FCSTD DOCUMENT  (FreeCAD 0.21R33668 +7 (Git))
Label: robot-main
License: All rights reserved
LicenseURL: https://en.wikipedia.org/wiki/All_rights_reserved
objects: App::Link×11
EXTERNAL_REF file=Off-the-shelf/BL-5C.FCStd obj=Body
EXTERNAL_REF file=robot-pcb.FCStd obj=LinkGroup
EXTERNAL_REF file=Off-the-shelf/GT2-220.FCStd obj=Body
EXTERNAL_REF file=Off-the-shelf/ball.FCStd obj=Body
EXTERNAL_REF file=robot-body.FCStd obj=Body
EXTERNAL_REF file=robot-idler.FCStd obj=LinkGroup
EXTERNAL_REF file=robot-motor-holder.FCStd obj=LinkGroup

FEATURE [App::Link] Link002  label="battery-t"
  LinkPlacement = pos=(-1.5,0,11.5) rot=(1,0,0;3.14159rad)
  LinkedObject = -> <external Off-the-shelf/BL-5C.FCStd>#Body
  Placement = pos=(-1.5,0,11.5) rot=(1,0,0;3.14159rad)
FEATURE [App::Link] Link003  label="battery-b"
  LinkPlacement = pos=(-1.5,0,-11.5) rot=(0,0,1;0rad)
  LinkedObject = -> <external Off-the-shelf/BL-5C.FCStd>#Body
  Placement = pos=(-1.5,0,-11.5) rot=(0,0,1;0rad)
FEATURE [App::Link] Link010  label="pcb"
  LinkPlacement = pos=(25,0,0) rot=(1,0,0;0rad)
  LinkedObject = -> <external robot-pcb.FCStd>#LinkGroup
  Placement = pos=(25,0,0) rot=(1,0,0;0rad)
FEATURE [App::Link] Link013  label="track-l"
  LinkPlacement = pos=(0,-30,0) rot=(0,0,1;0rad)
  LinkedObject = -> <external Off-the-shelf/GT2-220.FCStd>#Body
  Placement = pos=(0,-30,0) rot=(0,0,1;0rad)
FEATURE [App::Link] Link014  label="track-r"
  LinkPlacement = pos=(0,30,0) rot=(0,0,1;0rad)
  LinkedObject = -> <external Off-the-shelf/GT2-220.FCStd>#Body
  Placement = pos=(0,30,0) rot=(0,0,1;0rad)
FEATURE [App::Link] Link015  label="tt-ball"
  LinkPlacement = pos=(-40,0,0) rot=(0,0,1;0rad)
  LinkedObject = -> <external Off-the-shelf/ball.FCStd>#Body
  Placement = pos=(-40,0,0) rot=(0,0,1;0rad)
FEATURE [App::Link] Link016  label="body-main"
  LinkedObject = -> <external robot-body.FCStd>#Body
FEATURE [App::Link] Link019  label="idler-assy-l"
  LinkPlacement = pos=(50,-34,0) rot=(1,0,0;-1.5708rad)
  LinkedObject = -> <external robot-idler.FCStd>#LinkGroup
  Placement = pos=(50,-34,0) rot=(1,0,0;-1.5708rad)
FEATURE [App::Link] Link020  label="idler-assy-r"
  LinkPlacement = pos=(0,34,0) rot=(1,0,0;1.5708rad)
  LinkedObject = -> <external robot-idler.FCStd>#LinkGroup
  Placement = pos=(0,34,0) rot=(1,0,0;1.5708rad)
FEATURE [App::Link] Link  label="traction-assy-l"
  LinkPlacement = pos=(0,-14.9,0) rot=(0,0,1;0rad)
  LinkedObject = -> <external robot-motor-holder.FCStd>#LinkGroup
  Placement = pos=(0,-14.9,0) rot=(0,0,1;0rad)
FEATURE [App::Link] Link021  label="traction-assy-r"
  LinkPlacement = pos=(50,14.9,0) rot=(0,0,1;3.14159rad)
  LinkedObject = -> <external robot-motor-holder.FCStd>#LinkGroup
  Placement = pos=(50,14.9,0) rot=(0,0,1;3.14159rad)

RESOLVED EXTERNAL PARTS (link-assembly join: the EXTERNAL_REF files above that resolve inside this repo's crawl, each included once):
---- part Off-the-shelf/BL-5C.FCStd = doc fcstd_d717545ff7e7 ----
FCSTD DOCUMENT  (FreeCAD 0.21R33668 +7 (Git))
Label: BL-5C
License: All rights reserved
LicenseURL: https://en.wikipedia.org/wiki/All_rights_reserved
objects: Sketcher::SketchObject×2, PartDesign::Pad×1, PartDesign::Plane×1, PartDesign::Pocket×1, PartDesign::Body×1
note: 8 computed .brp shape members not serialized (recipe doc carries the construction recipe); baked Part::Feature solids carry a one-line shape summary decoded from their .brp

FEATURE [Sketcher::SketchObject] Sketch
  FullyConstrained = true
  MapMode = 5
  Placement = pos=(0,0,0) rot=(0.57735,0.57735,0.57735;2.0944rad)
  Support = -> [YZ_Plane]
  sketch-geometry (6):
    g0: ArcOfCircle CenterX=-14.15 CenterY=0 CenterZ=0 NormalX=0 NormalY=0 NormalZ=1 AngleXU=0 Radius=2.8 StartAngle=1.5708 EndAngle=4.71239
    g1: ArcOfCircle CenterX=14.15 CenterY=0 CenterZ=0 NormalX=0 NormalY=0 NormalZ=1 AngleXU=0 Radius=2.8 StartAngle=4.71239 EndAngle=7.85398
    g2: LineSegment StartX=-14.15 StartY=2.8 StartZ=0 EndX=14.15 EndY=2.8 EndZ=0
    g3: LineSegment StartX=-14.15 StartY=-2.8 StartZ=0 EndX=14.15 EndY=-2.8 EndZ=0
    g4: GeomPoint X=16.95 Y=0 Z=0
    g5: GeomPoint X=-16.95 Y=0 Z=0
  constraints (13):
    c: PointOnObject(g0,g-1)
    c: Horizontal(g2)
    c: Tangent(g2,g0) = 1.5708
    c: Tangent(g3,g0) = -1.5708
    c: Tangent(g3,g1) = -1.5708
    c: Tangent(g2,g1) = 1.5708
    c: PointOnObject(g4,g1)
    c: PointOnObject(g4,g-1)
    c: DistanceY(g1,g1) = 5.6
    c: Symmetric(g0,g1,g-1)
    c: PointOnObject(g5,g0)
    c: PointOnObject(g5,g-1)
    c: DistanceX(g5,g4) = 33.9
FEATURE [PartDesign::Pad] Pad
  Direction = (1,-2e-16,3e-16)
  Length = 53
  Length2 = 10
  Placement = pos=(0,0,0) rot=(0.57735,0.57735,0.57735;2.0944rad)
  Profile = -> Sketch
  ReferenceAxis = -> Sketch [N_Axis]
  Type = 0
FEATURE [PartDesign::Plane] DatumPlane
  Length = 60
  MapMode = 5
  Placement = pos=(0,0,0) rot=(0.57735,0.57735,-0.57735;4.18879rad)
  ResizeMode = 0
  Support = -> [Pad]
  Width = 60
FEATURE [Sketcher::SketchObject] Sketch001
  ExternalGeometry = -> [Pad]
  FullyConstrained = true
  MapMode = 5
  Placement = pos=(0,0,0) rot=(0.57735,0.57735,-0.57735;4.18879rad)
  Support = -> [DatumPlane]
  sketch-geometry (16):
    g0: LineSegment StartX=11.95 StartY=2.3 StartZ=0 EndX=13.95 EndY=2.3 EndZ=0
    g1: LineSegment StartX=13.95 StartY=2.3 StartZ=0 EndX=13.95 EndY=-2.3 EndZ=0
    g2: LineSegment StartX=13.95 StartY=-2.3 StartZ=0 EndX=11.95 EndY=-2.3 EndZ=0
    g3: LineSegment StartX=11.95 StartY=-2.3 StartZ=0 EndX=11.95 EndY=2.3 EndZ=0
    g4: LineSegment StartX=8.75 StartY=2.3 StartZ=0 EndX=10.75 EndY=2.3 EndZ=0
    g5: LineSegment StartX=10.75 StartY=2.3 StartZ=0 EndX=10.75 EndY=-2.3 EndZ=0
    g6: LineSegment StartX=10.75 StartY=-2.3 StartZ=0 EndX=8.75 EndY=-2.3 EndZ=0
    g7: LineSegment StartX=8.75 StartY=-2.3 StartZ=0 EndX=8.75 EndY=2.3 EndZ=0
    g8: LineSegment StartX=5.55 StartY=2.3 StartZ=0 EndX=7.55 EndY=2.3 EndZ=0
    g9: LineSegment StartX=7.55 StartY=2.3 StartZ=0 EndX=7.55 EndY=-2.3 EndZ=0
    g10: LineSegment StartX=7.55 StartY=-2.3 StartZ=0 EndX=5.55 EndY=-2.3 EndZ=0
    g11: LineSegment StartX=5.55 StartY=-2.3 StartZ=0 EndX=5.55 EndY=2.3 EndZ=0
    g12: LineSegment StartX=7.55 StartY=2.3 StartZ=0 EndX=8.75 EndY=2.3 EndZ=0
    g13: LineSegment StartX=10.75 StartY=2.3 StartZ=0 EndX=11.95 EndY=2.3 EndZ=0
    g14: GeomPoint X=-16.95 Y=0 Z=0
    g15: GeomPoint X=16.95 Y=0 Z=0
  constraints (43):
    c: Coincident(g0,g1)
    c: Coincident(g1,g2)
    c: Coincident(g2,g3)
    c: Coincident(g3,g0)
    c: Horizontal(g0)
    c: Horizontal(g2)
    c: Vertical(g3)
    c: Coincident(g4,g5)
    c: Coincident(g5,g6)
    c: Coincident(g6,g7)
    c: Coincident(g7,g4)
    c: Horizontal(g4)
    c: Horizontal(g6)
    c: Vertical(g5)
    c: Vertical(g7)
    c: Coincident(g8,g9)
    c: Coincident(g9,g10)
    c: Coincident(g10,g11)
    c: Coincident(g11,g8)
    c: Horizontal(g8)
    c: Horizontal(g10)
    c: Vertical(g9)
    c: Vertical(g11)
    c: PointOnObject(g4,g8)
    c: PointOnObject(g0,g8)
    c: PointOnObject(g6,g10)
    c: PointOnObject(g2,g10)
    c: Equal(g8,g4)
    c: Coincident(g12,g8)
    c: Coincident(g12,g4)
    c: Coincident(g13,g4)
    c: Coincident(g13,g0)
    c: Equal(g13,g12)
    c: PointOnObject(g14,g-3)
    c: PointOnObject(g14,g-1)
    c: DistanceX(g14,g10) = 22.5
    c: PointOnObject(g15,g-1)
    c: PointOnObject(g15,g-4)
    c: DistanceX(g1,g15) = 3
    c: DistanceX(g6,g6) = 2
    c: Equal(g2,g6)
    c: Symmetric(g0,g1,g-1)
    c: DistanceY(g1,g1) = 4.6
FEATURE [PartDesign::Pocket] Pocket
  BaseFeature = -> Pad
  Direction = (1,-4e-16,4e-16)
  Length = 0.6
  Length2 = 5
  Placement = pos=(0,0,0) rot=(0.57735,0.57735,0.57735;2.0944rad)
  Profile = -> Sketch001
  ReferenceAxis = -> Sketch001 [N_Axis]
  Type = 0
FEATURE [PartDesign::Body] Body  label="BL-5C"
  Group = -> [Sketch,Pad,DatumPlane,Sketch001,Pocket]
  Origin = -> Origin
  Tip = -> Pocket
---- part Off-the-shelf/GT2-220.FCStd = doc fcstd_4230f36f5c53 ----
FCSTD DOCUMENT  (FreeCAD 0.21R33668 +7 (Git))
Label: GT2-220
License: All rights reserved
LicenseURL: https://en.wikipedia.org/wiki/All_rights_reserved
objects: Sketcher::SketchObject×1, PartDesign::Pad×1, PartDesign::Body×1
note: 4 computed .brp shape members not serialized (recipe doc carries the construction recipe); baked Part::Feature solids carry a one-line shape summary decoded from their .brp

FEATURE [Sketcher::SketchObject] Sketch
  FullyConstrained = true
  MapMode = 5
  Placement = pos=(0,0,0) rot=(1,0,0;1.5708rad)
  Support = -> [XZ_Plane]
  sketch-geometry (10):
    g0: ArcOfCircle CenterX=0 CenterY=0 CenterZ=0 NormalX=0 NormalY=0 NormalZ=1 AngleXU=0 Radius=18 StartAngle=1.5708 EndAngle=4.71239
    g1: ArcOfCircle CenterX=47.6 CenterY=0 CenterZ=0 NormalX=0 NormalY=0 NormalZ=1 AngleXU=0 Radius=18 StartAngle=4.71239 EndAngle=7.85398
    g2: LineSegment StartX=1.1e-15 StartY=18 StartZ=0 EndX=47.6 EndY=18 EndZ=0
    g3: LineSegment StartX=-3.3e-15 StartY=-18 StartZ=0 EndX=47.6 EndY=-18 EndZ=0
    g4: Circle CenterX=0 CenterY=0 CenterZ=0 NormalX=0 NormalY=0 NormalZ=1 AngleXU=0 Radius=17
    g5: GeomPoint X=0 Y=17 Z=0
    g6: ArcOfCircle CenterX=0 CenterY=0 CenterZ=0 NormalX=0 NormalY=0 NormalZ=1 AngleXU=0 Radius=16.25 StartAngle=1.5708 EndAngle=4.71239
    g7: ArcOfCircle CenterX=47.6 CenterY=0 CenterZ=0 NormalX=0 NormalY=0 NormalZ=1 AngleXU=0 Radius=16.25 StartAngle=4.71239 EndAngle=7.85398
    g8: LineSegment StartX=1e-15 StartY=16.25 StartZ=0 EndX=47.6 EndY=16.25 EndZ=0
    g9: LineSegment StartX=-3e-15 StartY=-16.25 StartZ=0 EndX=47.6 EndY=-16.25 EndZ=0
  constraints (22):
    c: Coincident(g0,g-1)
    c: PointOnObject(g0,g-2)
    c: PointOnObject(g1,g-1)
    c: Coincident(g4,g0)
    c: PointOnObject(g5,g4)
    c: PointOnObject(g5,g-2)
    c: DistanceY(g5,g0) = 1
    c: DistanceX(g0,g1) = 47.6
    c: DistanceX(g0,g1) = 47.6
    c: Tangent(g2,g1) = 1.5708
    c: Tangent(g3,g1) = -1.5708
    c: Tangent(g3,g0) = -1.5708
    c: Tangent(g2,g0) = 1.5708
    c: Diameter(g4) = 34
    c: Coincident(g6,g0)
    c: PointOnObject(g6,g-2)
    c: Coincident(g7,g1)
    c: Tangent(g9,g7) = -1.5708
    c: Tangent(g8,g7) = 1.5708
    c: Tangent(g8,g6) = 1.5708
    c: Tangent(g9,g6) = -1.5708
    c: DistanceY(g6,g5) = 0.75
FEATURE [PartDesign::Pad] Pad
  Direction = (0,-1,-2e-16)
  Length = 15
  Length2 = 10
  Midplane = true
  Placement = pos=(0,0,0) rot=(1,0,0;1.5708rad)
  Profile = -> Sketch
  ReferenceAxis = -> Sketch [N_Axis]
  Type = 0
FEATURE [PartDesign::Body] Body  label="GT2-220"
  Group = -> [Sketch,Pad]
  Origin = -> Origin
  Tip = -> Pad
---- part Off-the-shelf/ball.FCStd = doc fcstd_e7537ce59ff1 ----
FCSTD DOCUMENT  (FreeCAD 0.21R33668 +7 (Git))
Label: ball
License: All rights reserved
LicenseURL: https://en.wikipedia.org/wiki/All_rights_reserved
objects: Sketcher::SketchObject×1, PartDesign::Revolution×1, PartDesign::Body×1
note: 4 computed .brp shape members not serialized (recipe doc carries the construction recipe); baked Part::Feature solids carry a one-line shape summary decoded from their .brp

FEATURE [Sketcher::SketchObject] Sketch
  FullyConstrained = true
  MapMode = 5
  Placement = pos=(0,0,0) rot=(1,0,0;1.5708rad)
  Support = -> [XZ_Plane]
  sketch-geometry (2):
    g0: ArcOfCircle CenterX=0 CenterY=0 CenterZ=0 NormalX=0 NormalY=0 NormalZ=1 AngleXU=0 Radius=20 StartAngle=1.5708 EndAngle=4.71239
    g1: LineSegment StartX=0 StartY=20 StartZ=0 EndX=0 EndY=-20 EndZ=0
  constraints (6):
    c: Coincident(g0,g-1)
    c: Coincident(g1,g0)
    c: Coincident(g1,g0)
    c: Vertical(g1)
    c: PointOnObject(g0,g1)
    c: DistanceY(g1,g1) = 40
FEATURE [PartDesign::Revolution] Revolution
  Angle = 360
  Axis = (0,2e-16,1)
  Base = (0,0,0)
  Placement = pos=(0,0,0) rot=(1,0,0;1.5708rad)
  Profile = -> Sketch
  ReferenceAxis = -> Sketch [V_Axis]
FEATURE [PartDesign::Body] Body  label="ball"
  Group = -> [Sketch,Revolution]
  Origin = -> Origin
  Tip = -> Revolution
---- part robot-body.FCStd = doc fcstd_04e413dc6602 ----
FCSTD DOCUMENT  (FreeCAD 0.21R33668 +7 (Git))
Label: robot-body
License: All rights reserved
LicenseURL: https://en.wikipedia.org/wiki/All_rights_reserved
objects: Sketcher::SketchObject×7, PartDesign::Pocket×5, PartDesign::Plane×3, PartDesign::Pad×1, PartDesign::Body×1
note: 23 computed .brp shape members not serialized (recipe doc carries the construction recipe); baked Part::Feature solids carry a one-line shape summary decoded from their .brp

FEATURE [Sketcher::SketchObject] Sketch
  FullyConstrained = true
  MapMode = 5
  Placement = pos=(0,0,0) rot=(1,0,0;1.5708rad)
  Support = -> [XZ_Plane]
  sketch-geometry (4):
    g0: ArcOfCircle CenterX=0 CenterY=0 CenterZ=0 NormalX=0 NormalY=0 NormalZ=1 AngleXU=0 Radius=18 StartAngle=1.5708 EndAngle=4.71239
    g1: ArcOfCircle CenterX=50 CenterY=0 CenterZ=0 NormalX=0 NormalY=0 NormalZ=1 AngleXU=0 Radius=18 StartAngle=4.71239 EndAngle=7.85398
    g2: LineSegment StartX=1.1e-15 StartY=18 StartZ=0 EndX=50 EndY=18 EndZ=0
    g3: LineSegment StartX=0 StartY=-18 StartZ=0 EndX=50 EndY=-18 EndZ=0
  constraints (9):
    c: Coincident(g0,g-1)
    c: PointOnObject(g0,g-2)
    c: PointOnObject(g1,g-1)
    c: Tangent(g3,g0) = -1.5708
    c: Tangent(g2,g0) = 1.5708
    c: Tangent(g2,g1) = 1.5708
    c: Tangent(g3,g1) = -1.5708
    c: DistanceX(g0,g1) = 50
    c: Diameter(g0) = 36
FEATURE [PartDesign::Pad] Pad
  Direction = (0,-1,-2e-16)
  Length = 40
  Length2 = 10
  Midplane = true
  Placement = pos=(0,0,0) rot=(1,0,0;1.5708rad)
  Profile = -> Sketch
  ReferenceAxis = -> Sketch [N_Axis]
  Type = 0
FEATURE [Sketcher::SketchObject] Sketch001
  FullyConstrained = true
  MapMode = 5
  Support = -> [XY_Plane]
  sketch-geometry (2):
    g0: Circle CenterX=-35 CenterY=0 CenterZ=0 NormalX=0 NormalY=0 NormalZ=1 AngleXU=0 Radius=25
    g1: Circle CenterX=85 CenterY=0 CenterZ=0 NormalX=0 NormalY=0 NormalZ=1 AngleXU=0 Radius=25
  constraints (6):
    c: PointOnObject(g0,g-1)
    c: PointOnObject(g1,g-1)
    c: Equal(g1,g0)
    c: DistanceX(g0,g-1) = 35
    c: DistanceX(g-1,g1) = 85
    c: Diameter(g0) = 50
FEATURE [PartDesign::Pocket] Pocket
  BaseFeature = -> Pad
  Direction = (0,0,-1)
  Length = 5
  Length2 = 5
  Midplane = true
  Placement = pos=(0,0,0) rot=(1,0,0;1.5708rad)
  Profile = -> Sketch001
  ReferenceAxis = -> Sketch001 [N_Axis]
  Type = 1
FEATURE [PartDesign::Plane] DatumPlane
  Length = 106.638
  MapMode = 5
  ResizeMode = 0
  Support = -> [XY_Plane]
  Width = 63.6382
FEATURE [Sketcher::SketchObject] Sketch002
  FullyConstrained = true
  MapMode = 5
  Support = -> [DatumPlane]
  sketch-geometry (7):
    g0: ArcOfCircle CenterX=-35 CenterY=0 CenterZ=0 NormalX=0 NormalY=0 NormalZ=1 AngleXU=0 Radius=27.5 StartAngle=5.73706 EndAngle=6.82931
    g1: LineSegment StartX=-11.5 StartY=20 StartZ=0 EndX=55 EndY=20 EndZ=0
    g2: LineSegment StartX=-11.5 StartY=-20 StartZ=0 EndX=55 EndY=-20 EndZ=0
    g3: LineSegment StartX=-11.5 StartY=20 StartZ=0 EndX=-11.5 EndY=14.2829 EndZ=0
    g4: LineSegment StartX=-11.5 StartY=-14.2829 StartZ=0 EndX=-11.5 EndY=-20 EndZ=0
    g5: LineSegment StartX=55 StartY=20 StartZ=0 EndX=55 EndY=-20 EndZ=0
    g6: LineSegment StartX=-7.5 StartY=20 StartZ=0 EndX=-7.5 EndY=-20 EndZ=0
  constraints (23):
    c: PointOnObject(g0,g-1)
    c: Horizontal(g1)
    c: Horizontal(g2)
    c: Coincident(g3,g1)
    c: Coincident(g3,g0)
    c: Vertical(g3)
    c: Coincident(g4,g0)
    c: Coincident(g4,g2)
    c: Vertical(g4)
    c: Coincident(g5,g1)
    c: Coincident(g5,g2)
    c: Vertical(g5)
    c: Equal(g3,g4)
    c: DistanceY(g2,g1) = 40
    c: DistanceX(g-1,g1) = 55
    c: PointOnObject(g6,g1)
    c: PointOnObject(g6,g2)
    c: Vertical(g6)
    c: Tangent(g6,g0)
    c: DistanceX(g1,g6) = 4
    c: Equal(g2,g1)
    c: Radius(g0) = 27.5
    c: DistanceX(g0,g-1) = 35
FEATURE [PartDesign::Pocket] Pocket001
  BaseFeature = -> Pocket
  Direction = (0,0,-1)
  Length = 19
  Length2 = 5
  Midplane = true
  Placement = pos=(0,0,0) rot=(1,0,0;1.5708rad)
  Profile = -> Sketch002
  ReferenceAxis = -> Sketch002 [N_Axis]
  Type = 0
FEATURE [PartDesign::Plane] DatumPlane001
  Length = 60
  MapMode = 5
  Placement = pos=(0,0,0) rot=(0.57735,0.57735,0.57735;2.0944rad)
  ResizeMode = 0
  Support = -> [YZ_Plane]
  Width = 60
FEATURE [Sketcher::SketchObject] Sketch003
  FullyConstrained = true
  MapMode = 5
  Placement = pos=(0,0,0) rot=(0.57735,0.57735,0.57735;2.0944rad)
  Support = -> [DatumPlane001]
  sketch-geometry (12):
    g0: LineSegment StartX=-20 StartY=9 StartZ=0 EndX=-16 EndY=15 EndZ=0
    g1: LineSegment StartX=-16 StartY=15 StartZ=0 EndX=16 EndY=15 EndZ=0
    g2: LineSegment StartX=16 StartY=15 StartZ=0 EndX=20 EndY=9 EndZ=0
    g3: LineSegment StartX=20 StartY=9 StartZ=0 EndX=20 EndY=-9 EndZ=0
    g4: LineSegment StartX=20 StartY=-9 StartZ=0 EndX=16 EndY=-15 EndZ=0
    g5: LineSegment StartX=16 StartY=-15 StartZ=0 EndX=-16 EndY=-15 EndZ=0
    g6: LineSegment StartX=-16 StartY=-15 StartZ=0 EndX=-20 EndY=-9 EndZ=0
    g7: LineSegment StartX=-20 StartY=-9 StartZ=0 EndX=-20 EndY=9 EndZ=0
    g8: LineSegment StartX=-16 StartY=15 StartZ=0 EndX=-16 EndY=-15 EndZ=0
    g9: LineSegment StartX=16 StartY=15 StartZ=0 EndX=16 EndY=-15 EndZ=0
    g10: LineSegment StartX=-20 StartY=9 StartZ=0 EndX=20 EndY=9 EndZ=0
    g11: LineSegment StartX=-20 StartY=-9 StartZ=0 EndX=20 EndY=-9 EndZ=0
  constraints (30):
    c: Coincident(g0,g1)
    c: Horizontal(g1)
    c: Coincident(g1,g2)
    c: Coincident(g2,g3)
    c: Vertical(g3)
    c: Coincident(g3,g4)
    c: Coincident(g4,g5)
    c: Horizontal(g5)
    c: Coincident(g5,g6)
    c: Coincident(g6,g7)
    c: Coincident(g7,g0)
    c: Vertical(g7)
    c: Coincident(g8,g0)
    c: Coincident(g8,g5)
    c: Vertical(g8)
    c: Coincident(g9,g1)
    c: Coincident(g9,g4)
    c: Vertical(g9)
    c: Coincident(g10,g0)
    c: Coincident(g10,g2)
    c: Horizontal(g10)
    c: Coincident(g11,g6)
    c: Coincident(g11,g3)
    c: Horizontal(g11)
    c: DistanceX(g10,g10) = 40
    c: Symmetric(g0,g3,g-1)
    c: Symmetric(g1,g5,g-1)
    c: DistanceY(g4,g1) = 30
    c: DistanceX(g5,g5) = 32
    c: DistanceY(g3,g3) = 18
FEATURE [PartDesign::Pocket] Pocket002
  BaseFeature = -> Pocket001
  Direction = (-1,1e-16,-1e-16)
  Length = 3
  Length2 = 55
  Placement = pos=(0,0,0) rot=(1,0,0;1.5708rad)
  Profile = -> Sketch003
  ReferenceAxis = -> Sketch003 [N_Axis]
  Type = 4
FEATURE [Sketcher::SketchObject] Sketch004
  FullyConstrained = true
  MapMode = 5
  Placement = pos=(0,0,0) rot=(0.57735,0.57735,0.57735;2.0944rad)
  Support = -> [DatumPlane001]
FEATURE [PartDesign::Plane] DatumPlane002
  AttachmentOffset = pos=(0,0,-2) rot=(0,0,1;0rad)
  Length = 60
  MapMode = 5
  Placement = pos=(-2,2e-16,-2e-16) rot=(0.57735,0.57735,0.57735;2.0944rad)
  ResizeMode = 0
  Support = -> [DatumPlane001]
  Width = 60
FEATURE [Sketcher::SketchObject] Sketch005
  FullyConstrained = true
  MapMode = 5
  Placement = pos=(-2,2e-16,-2e-16) rot=(0.57735,0.57735,0.57735;2.0944rad)
  Support = -> [DatumPlane002]
  sketch-geometry (8):
    g0: LineSegment StartX=-17 StartY=16 StartZ=0 EndX=-2 EndY=16 EndZ=0
    g1: LineSegment StartX=-2 StartY=16 StartZ=0 EndX=1 EndY=9.5 EndZ=0
    g2: LineSegment StartX=1 StartY=9.5 StartZ=0 EndX=-20 EndY=9.5 EndZ=0
    g3: LineSegment StartX=-20 StartY=9.5 StartZ=0 EndX=-17 EndY=16 EndZ=0
    g4: LineSegment StartX=-1 StartY=-9.5 StartZ=0 EndX=20 EndY=-9.5 EndZ=0
    g5: LineSegment StartX=20 StartY=-9.5 StartZ=0 EndX=17 EndY=-16 EndZ=0
    g6: LineSegment StartX=17 StartY=-16 StartZ=0 EndX=2 EndY=-16 EndZ=0
    g7: LineSegment StartX=2 StartY=-16 StartZ=0 EndX=-1 EndY=-9.5 EndZ=0
  constraints (22):
    c: Coincident(g0,g1)
    c: Coincident(g1,g2)
    c: Coincident(g2,g3)
    c: Coincident(g3,g0)
    c: Horizontal(g0)
    c: Horizontal(g2)
    c: DistanceY(g-1,g1) = 9.5
    c: DistanceY(g1,g1) = 6.5
    c: Coincident(g4,g5)
    c: Coincident(g5,g6)
    c: Coincident(g6,g7)
    c: Coincident(g7,g4)
    c: Horizontal(g4)
    c: Horizontal(g6)
    c: Symmetric(g4,g1,g-1)
    c: Symmetric(g5,g0,g-1)
    c: DistanceX(g0,g-1) = 17
    c: DistanceX(g2,g-1) = 20
    c: DistanceX(g0,g-1) = 2
    c: Equal(g1,g3)
    c: Equal(g7,g5)
    c: Equal(g5,g1)
FEATURE [PartDesign::Pocket] Pocket003
  BaseFeature = -> Pocket002
  Direction = (-1,0,0)
  Length = 4.5
  Length2 = 5
  Placement = pos=(0,0,0) rot=(1,0,0;1.5708rad)
  Profile = -> Sketch005
  ReferenceAxis = -> Sketch005 [N_Axis]
  Type = 0
FEATURE [Sketcher::SketchObject] Sketch006
  FullyConstrained = false
  MapMode = 5
  Placement = pos=(0,0,0) rot=(1,0,0;1.5708rad)
  Support = -> [XZ_Plane]
  sketch-geometry (4):
    g0: LineSegment StartX=53.8225 StartY=25.8556 StartZ=0 EndX=83.8227 EndY=25.8556 EndZ=0
    g1: LineSegment StartX=83.8227 StartY=25.8556 StartZ=0 EndX=83.8227 EndY=-24.1322 EndZ=0
    g2: LineSegment StartX=83.8227 StartY=-24.1322 StartZ=0 EndX=53.8225 EndY=-24.1322 EndZ=0
    g3: LineSegment StartX=53.8225 StartY=-24.1322 StartZ=0 EndX=53.8225 EndY=25.8556 EndZ=0
  constraints (8):
    c: Coincident(g0,g1)
    c: Coincident(g1,g2)
    c: Coincident(g2,g3)
    c: Coincident(g3,g0)
    c: Horizontal(g0)
    c: Horizontal(g2)
    c: Vertical(g1)
    c: Vertical(g3)
FEATURE [PartDesign::Pocket] Pocket004
  BaseFeature = -> Pocket003
  Direction = (0,1,2e-16)
  Length = 5
  Length2 = 5
  Midplane = true
  Placement = pos=(0,0,0) rot=(1,0,0;1.5708rad)
  Profile = -> Sketch006
  ReferenceAxis = -> Sketch006 [N_Axis]
  Type = 1
FEATURE [PartDesign::Body] Body  label="body-main"
  Group = -> [Sketch,Pad,Sketch001,Pocket,DatumPlane,Sketch002,Pocket001,DatumPlane001,Sketch003,Pocket002,Sketch004,DatumPlane002,Sketch005,Pocket003,Sketch006,Pocket004]
  Origin = -> Origin
  Tip = -> Pocket004
---- part robot-idler.FCStd = doc fcstd_2a472838672f ----
FCSTD DOCUMENT  (FreeCAD 0.21R33668 +7 (Git))
Label: robot-idler
License: All rights reserved
LicenseURL: https://en.wikipedia.org/wiki/All_rights_reserved
objects: Sketcher::SketchObject×8, PartDesign::Plane×3, PartDesign::Revolution×2, PartDesign::Body×2, PartDesign::Pad×2, App::Link×1, PartDesign::Chamfer×1, PartDesign::AdditiveLoft×1, PartDesign::Pocket×1, App::LinkGroup×1
note: 27 computed .brp shape members not serialized (recipe doc carries the construction recipe); baked Part::Feature solids carry a one-line shape summary decoded from their .brp
EXTERNAL_REF file=Off-the-shelf/608.FCStd obj=Body

FEATURE [Sketcher::SketchObject] Sketch
  FullyConstrained = true
  MapMode = 5
  Placement = pos=(0,0,0) rot=(0.57735,0.57735,0.57735;2.0944rad)
  Support = -> [YZ_Plane]
  sketch-geometry (10):
    g0: LineSegment StartX=9.6 StartY=11.2 StartZ=0 EndX=9.6 EndY=10.7 EndZ=0
    g1: LineSegment StartX=9.6 StartY=10.7 StartZ=0 EndX=11.1 EndY=9.2 EndZ=0
    g2: LineSegment StartX=11.1 StartY=9.2 StartZ=0 EndX=11.1 EndY=2 EndZ=0
    g3: LineSegment StartX=11.1 StartY=2 StartZ=0 EndX=9.6 EndY=1.73551 EndZ=0
    g4: LineSegment StartX=9.6 StartY=1.73551 StartZ=0 EndX=10.602 EndY=0 EndZ=0
    g5: LineSegment StartX=10.602 StartY=0 StartZ=0 EndX=17 EndY=0 EndZ=0
    g6: LineSegment StartX=17 StartY=0 StartZ=0 EndX=17 EndY=11.2 EndZ=0
    g7: LineSegment StartX=17 StartY=11.2 StartZ=0 EndX=9.6 EndY=11.2 EndZ=0
    g8: LineSegment StartX=9.6 StartY=1.73551 StartZ=0 EndX=17 EndY=1.73551 EndZ=0
    g9: LineSegment StartX=11.1 StartY=9.2 StartZ=0 EndX=17 EndY=9.2 EndZ=0
  constraints (31):
    c: Vertical(g0)
    c: Coincident(g0,g1)
    c: Coincident(g1,g2)
    c: Vertical(g2)
    c: Coincident(g2,g3)
    c: Coincident(g3,g4)
    c: PointOnObject(g4,g-1)
    c: Coincident(g4,g5)
    c: PointOnObject(g5,g-1)
    c: Coincident(g5,g6)
    c: Vertical(g6)
    c: Coincident(g6,g7)
    c: Coincident(g7,g0)
    c: Horizontal(g7)
    c: DistanceX(g-1,g5) = 17
    c: DistanceY(g5,g2) = 2
    c: Coincident(g8,g3)
    c: PointOnObject(g8,g6)
    c: Horizontal(g8)
    c: Angle(g8,g3) = 0.174533
    c: DistanceX(g-1,g2) = 11.1
    c: DistanceY(g2,g2) = 7.2
    c: DistanceX(g0,g1) = 1.5
    c: Coincident(g9,g1)
    c: PointOnObject(g9,g6)
    c: Horizontal(g9)
    c: Angle(g1,g9) = 3.92699
    c: DistanceY(g1,g6) = 2
    c: DistanceX(g3,g2) = 1.5
    c: Angle(g5,g4) = 2.0944
    c: DistanceY(g6,g6) = 11.2
FEATURE [PartDesign::Revolution] Revolution
  Angle = 360
  Axis = (-2e-16,3e-16,1)
  Base = (0,0,0)
  Placement = pos=(0,0,0) rot=(0.57735,0.57735,0.57735;2.0944rad)
  Profile = -> Sketch
  ReferenceAxis = -> Sketch [V_Axis]
  Reversed = true
FEATURE [Sketcher::SketchObject] Sketch001
  FullyConstrained = true
  MapMode = 5
  Placement = pos=(0,0,0) rot=(0.57735,0.57735,0.57735;2.0944rad)
  Support = -> [YZ_Plane001]
  sketch-geometry (10):
    g0: LineSegment StartX=0 StartY=0 StartZ=0 EndX=3.5 EndY=0 EndZ=0
    g1: LineSegment StartX=3.5 StartY=0 StartZ=0 EndX=4.58497 EndY=1.87922 EndZ=0
    g2: LineSegment StartX=4.58497 StartY=1.87922 StartZ=0 EndX=3.9 EndY=2 EndZ=0
    g3: LineSegment StartX=3.9 StartY=2 StartZ=0 EndX=3.9 EndY=9.2 EndZ=0
    g4: LineSegment StartX=3.9 StartY=9.2 StartZ=0 EndX=5 EndY=10.3 EndZ=0
    g5: LineSegment StartX=5 StartY=10.3 StartZ=0 EndX=5 EndY=11 EndZ=0
    g6: LineSegment StartX=5 StartY=11 StartZ=0 EndX=0 EndY=11 EndZ=0
    g7: LineSegment StartX=0 StartY=11 StartZ=0 EndX=0 EndY=0 EndZ=0
    g8: LineSegment StartX=3.9 StartY=2 StartZ=0 EndX=0 EndY=2 EndZ=0
    g9: LineSegment StartX=3.9 StartY=9.2 StartZ=0 EndX=0 EndY=9.2 EndZ=0
  constraints (29):
    c: Coincident(g-1,g0)
    c: PointOnObject(g0,g-1)
    c: Coincident(g0,g1)
    c: Coincident(g1,g2)
    c: Coincident(g2,g3)
    c: Vertical(g3)
    c: Coincident(g3,g4)
    c: Coincident(g4,g5)
    c: Vertical(g5)
    c: Coincident(g5,g6)
    c: PointOnObject(g6,g-2)
    c: Horizontal(g6)
    c: Coincident(g6,g7)
    c: Coincident(g7,g0)
    c: DistanceX(g0,g0) = 3.5
    c: Angle(g1,g0) = 2.0944
    c: DistanceY(g0,g2) = 2
    c: DistanceX(g6,g3) = 3.9
    c: DistanceY(g3,g3) = 7.2
    c: Coincident(g8,g2)
    c: PointOnObject(g8,g7)
    c: Horizontal(g8)
    c: Angle(g8,g2) = 2.96706
    c: Coincident(g9,g3)
    c: PointOnObject(g9,g7)
    c: Horizontal(g9)
    c: Angle(g4,g9) = 2.35619
    c: DistanceX(g6,g6) = 5
    c: DistanceY(g0,g5) = 11
FEATURE [PartDesign::Revolution] Revolution001
  Angle = 360
  Axis = (-2e-16,3e-16,1)
  Base = (0,0,0)
  Placement = pos=(0,0,0) rot=(0.57735,0.57735,0.57735;2.0944rad)
  Profile = -> Sketch001
  ReferenceAxis = -> Sketch001 [V_Axis]
  Reversed = true
FEATURE [App::Link] Link  label="bearing"
  LinkPlacement = pos=(0,0,5.6) rot=(1,0,0;1.5708rad)
  LinkedObject = -> <external Off-the-shelf/608.FCStd>#Body
  Placement = pos=(0,0,5.6) rot=(1,0,0;1.5708rad)
FEATURE [PartDesign::Chamfer] Chamfer
  Angle = 45
  Base = -> Revolution [Face6]
  BaseFeature = -> Revolution
  ChamferType = 0
  FlipDirection = false
  Placement = pos=(0,0,0) rot=(0.57735,0.57735,0.57735;2.0944rad)
  Size = 0.5
  Size2 = 1
  SupportTransform = false
  UseAllEdges = false
FEATURE [PartDesign::Body] Body  label="outer"
  Group = -> [Sketch,Revolution,Chamfer]
  Origin = -> Origin
  Tip = -> Chamfer
FEATURE [PartDesign::Plane] DatumPlane
  Length = 60
  MapMode = 5
  Placement = pos=(-4.8e-15,3.1e-15,11) rot=(0,0,-1;1.5708rad)
  ResizeMode = 0
  Support = -> [Revolution001]
  Width = 60
FEATURE [Sketcher::SketchObject] Sketch002
  FullyConstrained = true
  MapMode = 5
  Placement = pos=(-4.8e-15,3.1e-15,11) rot=(0,0,-1;1.5708rad)
  Support = -> [DatumPlane]
  sketch-geometry (1):
    g0: Circle CenterX=0 CenterY=0 CenterZ=0 NormalX=0 NormalY=0 NormalZ=1 AngleXU=0 Radius=5
  constraints (2):
    c: Coincident(g0,g-1)
    c: Diameter(g0) = 10
FEATURE [PartDesign::Plane] DatumPlane001
  AttachmentOffset = pos=(0,0,3) rot=(0,0,1;0rad)
  Length = 60
  MapMode = 5
  Placement = pos=(-6.2e-15,3.9e-15,14) rot=(0,0,-1;1.5708rad)
  ResizeMode = 0
  Support = -> [DatumPlane]
  Width = 60
FEATURE [Sketcher::SketchObject] Sketch003
  FullyConstrained = true
  MapMode = 5
  Placement = pos=(-6.2e-15,3.9e-15,14) rot=(0,0,-1;1.5708rad)
  Support = -> [DatumPlane001]
  sketch-geometry (4):
    g0: LineSegment StartX=-7 StartY=10 StartZ=0 EndX=7 EndY=10 EndZ=0
    g1: LineSegment StartX=7 StartY=10 StartZ=0 EndX=7 EndY=-1 EndZ=0
    g2: LineSegment StartX=7 StartY=-1 StartZ=0 EndX=-7 EndY=-1 EndZ=0
    g3: LineSegment StartX=-7 StartY=-1 StartZ=0 EndX=-7 EndY=10 EndZ=0
  constraints (11):
    c: Coincident(g0,g1)
    c: Coincident(g1,g2)
    c: Coincident(g2,g3)
    c: Coincident(g3,g0)
    c: Horizontal(g2)
    c: Vertical(g1)
    c: Symmetric(g0,g0,g-2)
    c: Vertical(g3)
    c: DistanceY(g-1,g0) = 10
    c: DistanceX(g0,g0) = 14
    c: DistanceY(g1,g-1) = 1
FEATURE [PartDesign::Plane] DatumPlane002
  AttachmentOffset = pos=(0,0,10) rot=(0,0,1;0rad)
  Length = 60
  MapMode = 5
  Placement = pos=(-1.06e-14,6.7e-15,24) rot=(0,0,-1;1.5708rad)
  ResizeMode = 0
  Support = -> [DatumPlane001]
  Width = 60
FEATURE [Sketcher::SketchObject] Sketch004
  FullyConstrained = true
  MapMode = 5
  Placement = pos=(-1.06e-14,6.7e-15,24) rot=(0,0,-1;1.5708rad)
  Support = -> [DatumPlane002]
  sketch-geometry (4):
    g0: LineSegment StartX=-7 StartY=10 StartZ=0 EndX=7 EndY=10 EndZ=0
    g1: LineSegment StartX=7 StartY=10 StartZ=0 EndX=7 EndY=-1 EndZ=0
    g2: LineSegment StartX=7 StartY=-1 StartZ=0 EndX=-7 EndY=-1 EndZ=0
    g3: LineSegment StartX=-7 StartY=-1 StartZ=0 EndX=-7 EndY=10 EndZ=0
  constraints (11):
    c: Coincident(g0,g1)
    c: Coincident(g1,g2)
    c: Coincident(g2,g3)
    c: Coincident(g3,g0)
    c: Horizontal(g2)
    c: Vertical(g1)
    c: Vertical(g3)
    c: DistanceX(g0,g0) = 14
    c: Symmetric(g0,g0,g-2)
    c: DistanceY(g-1,g0) = 10
    c: DistanceY(g1,g-1) = 1
FEATURE [PartDesign::AdditiveLoft] AdditiveLoft
  BaseFeature = -> Revolution001
  Closed = false
  Placement = pos=(0,0,0) rot=(0.57735,0.57735,0.57735;2.0944rad)
  Profile = -> Sketch002
  Ruled = true
  Sections = -> [Sketch003,Sketch004]
FEATURE [Sketcher::SketchObject] Sketch005
  FullyConstrained = true
  MapMode = 5
  Placement = pos=(0,0,0) rot=(0.57735,0.57735,0.57735;2.0944rad)
  Support = -> [YZ_Plane001]
  sketch-geometry (8):
    g0: LineSegment StartX=-7 StartY=20.35 StartZ=0 EndX=-9.33827 EndY=19 EndZ=0
    g1: LineSegment StartX=-9.33827 StartY=19 StartZ=0 EndX=-7 EndY=17.65 EndZ=0
    g2: LineSegment StartX=-7 StartY=17.65 StartZ=0 EndX=7 EndY=17.65 EndZ=0
    g3: LineSegment StartX=7 StartY=17.65 StartZ=0 EndX=9.33827 EndY=19 EndZ=0
    g4: LineSegment StartX=9.33827 StartY=19 StartZ=0 EndX=7 EndY=20.35 EndZ=0
    g5: LineSegment StartX=7 StartY=20.35 StartZ=0 EndX=-7 EndY=20.35 EndZ=0
    g6: LineSegment StartX=-7 StartY=20.35 StartZ=0 EndX=-7 EndY=17.65 EndZ=0
    g7: LineSegment StartX=7 StartY=20.35 StartZ=0 EndX=7 EndY=17.65 EndZ=0
  constraints (21):
    c: Coincident(g0,g1)
    c: Coincident(g1,g2)
    c: Horizontal(g2)
    c: Coincident(g2,g3)
    c: Coincident(g3,g4)
    c: Coincident(g4,g5)
    c: Coincident(g5,g0)
    c: Coincident(g6,g0)
    c: Coincident(g6,g1)
    c: Vertical(g6)
    c: Coincident(g7,g4)
    c: Coincident(g7,g2)
    c: Vertical(g7)
    c: Equal(g0,g1)
    c: Equal(g4,g3)
    c: Equal(g1,g3)
    c: Symmetric(g0,g4,g-2)
    c: Equal(g1,g6)
    c: DistanceX(g5,g5) = 14
    c: DistanceY(g2,g4) = 2.7
    c: DistanceY(g-1,g3) = 19
FEATURE [PartDesign::Pad] Pad
  BaseFeature = -> AdditiveLoft
  Direction = (1,-2e-16,3e-16)
  Length = 9
  Length2 = 10
  Placement = pos=(0,0,0) rot=(0.57735,0.57735,0.57735;2.0944rad)
  Profile = -> Sketch005
  ReferenceAxis = -> Sketch005 [N_Axis]
  Type = 0
FEATURE [Sketcher::SketchObject] Sketch006
  FullyConstrained = true
  MapMode = 5
  Placement = pos=(0,0,0) rot=(1,0,0;1.5708rad)
  Support = -> [XZ_Plane001]
  sketch-geometry (1):
    g0: Circle CenterX=4.5 CenterY=19 CenterZ=0 NormalX=0 NormalY=0 NormalZ=1 AngleXU=0 Radius=1.75
  constraints (3):
    c: Diameter(g0) = 3.5
    c: DistanceY(g-1,g0) = 19
    c: DistanceX(g-1,g0) = 4.5
FEATURE [PartDesign::Pocket] Pocket
  BaseFeature = -> Pad
  Direction = (0,1,2e-16)
  Length = 5
  Length2 = 5
  Midplane = true
  Placement = pos=(0,0,0) rot=(0.57735,0.57735,0.57735;2.0944rad)
  Profile = -> Sketch006
  ReferenceAxis = -> Sketch006 [N_Axis]
  Type = 1
FEATURE [Sketcher::SketchObject] Sketch007
  FullyConstrained = true
  MapMode = 5
  Support = -> [XY_Plane001]
  sketch-geometry (21):
    g0: LineSegment StartX=12 StartY=0.5 StartZ=0 EndX=3 EndY=0.5 EndZ=0
    g1: LineSegment StartX=3 StartY=0.5 StartZ=0 EndX=3 EndY=-0.5 EndZ=0
    g2: LineSegment StartX=3 StartY=-0.5 StartZ=0 EndX=12 EndY=-0.5 EndZ=0
    g3: LineSegment StartX=12 StartY=-0.5 StartZ=0 EndX=12 EndY=0.5 EndZ=0
    g4: LineSegment StartX=0.5 StartY=12 StartZ=0 EndX=-0.5 EndY=12 EndZ=0
    g5: LineSegment StartX=-0.5 StartY=12 StartZ=0 EndX=-0.5 EndY=3 EndZ=0
    g6: LineSegment StartX=-0.5 StartY=3 StartZ=0 EndX=0.5 EndY=3 EndZ=0
    g7: LineSegment StartX=0.5 StartY=3 StartZ=0 EndX=0.5 EndY=12 EndZ=0
    g8: LineSegment StartX=-3 StartY=0.5 StartZ=0 EndX=-12 EndY=0.5 EndZ=0
    g9: LineSegment StartX=-12 StartY=0.5 StartZ=0 EndX=-12 EndY=-0.5 EndZ=0
    g10: LineSegment StartX=-12 StartY=-0.5 StartZ=0 EndX=-3 EndY=-0.5 EndZ=0
    g11: LineSegment StartX=-3 StartY=-0.5 StartZ=0 EndX=-3 EndY=0.5 EndZ=0
    g12: LineSegment StartX=0.5 StartY=-3 StartZ=0 EndX=-0.5 EndY=-3 EndZ=0
    g13: LineSegment StartX=-0.5 StartY=-3 StartZ=0 EndX=-0.5 EndY=-12 EndZ=0
    g14: LineSegment StartX=-0.5 StartY=-12 StartZ=0 EndX=0.5 EndY=-12 EndZ=0
    g15: LineSegment StartX=0.5 StartY=-12 StartZ=0 EndX=0.5 EndY=-3 EndZ=0
    g16: Circle CenterX=0 CenterY=0 CenterZ=0 NormalX=0 NormalY=0 NormalZ=1 AngleXU=0 Radius=3
    g17: LineSegment StartX=3 StartY=0.5 StartZ=0 EndX=0.5 EndY=3 EndZ=0
    g18: LineSegment StartX=-0.5 StartY=3 StartZ=0 EndX=-3 EndY=0.5 EndZ=0
    g19: LineSegment StartX=-3 StartY=-0.5 StartZ=0 EndX=-0.5 EndY=-3 EndZ=0
    g20: LineSegment StartX=0.5 StartY=-3 StartZ=0 EndX=3 EndY=-0.5 EndZ=0
  constraints (54):
    c: Coincident(g0,g1)
    c: Coincident(g1,g2)
    c: Coincident(g2,g3)
    c: Coincident(g3,g0)
    c: Horizontal(g0)
    c: Horizontal(g2)
    c: Vertical(g3)
    c: Coincident(g4,g5)
    c: Coincident(g5,g6)
    c: Coincident(g6,g7)
    c: Coincident(g7,g4)
    c: Horizontal(g4)
    c: Vertical(g5)
    c: Vertical(g7)
    c: Coincident(g8,g9)
    c: Coincident(g9,g10)
    c: Coincident(g10,g11)
    c: Coincident(g11,g8)
    c: Horizontal(g8)
    c: Horizontal(g10)
    c: Vertical(g9)
    c: Coincident(g12,g13)
    c: Coincident(g13,g14)
    c: Coincident(g14,g15)
    c: Coincident(g15,g12)
    c: Horizontal(g14)
    c: Vertical(g13)
    c: Vertical(g15)
    c: Symmetric(g8,g10,g-1)
    c: Symmetric(g0,g1,g-1)
    c: Symmetric(g6,g5,g-2)
    c: Symmetric(g12,g12,g-2)
    c: Equal(g1,g11)
    c: Equal(g11,g6)
    c: Equal(g6,g12)
    c: DistanceY(g9,g9) = 1
    c: Coincident(g16,g-1)
    c: Tangent(g16,g6)
    c: Tangent(g16,g11)
    c: Tangent(g16,g12)
    c: Tangent(g1,g16)
    c: Diameter(g16) = 6
    c: Equal(g10,g5)
    c: Equal(g5,g2)
    c: Equal(g2,g13)
    c: DistanceX(g10,g10) = 9
    c: Coincident(g17,g0)
    c: Coincident(g17,g7)
    c: Coincident(g18,g5)
    c: Coincident(g18,g8)
    c: Coincident(g19,g10)
    c: Coincident(g19,g13)
    c: Coincident(g20,g15)
    c: Coincident(g20,g2)
FEATURE [PartDesign::Pad] Pad001
  BaseFeature = -> Pocket
  Direction = (0,0,1)
  Length = 0.2
  Length2 = 10
  Placement = pos=(0,0,0) rot=(0.57735,0.57735,0.57735;2.0944rad)
  Profile = -> Sketch007
  ReferenceAxis = -> Sketch007 [N_Axis]
  Type = 0
FEATURE [PartDesign::Body] Body001  label="inner"
  Group = -> [Sketch001,Revolution001,DatumPlane,Sketch002,DatumPlane001,Sketch003,DatumPlane002,Sketch004,AdditiveLoft,Sketch005,Pad,Sketch006,Pocket,Sketch007,Pad001]
  Origin = -> Origin001
  Tip = -> Pad001
FEATURE [App::LinkGroup] LinkGroup  label="idler-assy"
  ElementList = -> [Link,Body001,Body]
  LinkMode = 1
---- part robot-motor-holder.FCStd = doc fcstd_fcf45d935370 ----
FCSTD DOCUMENT  (FreeCAD 0.21R33668 +7 (Git))
Label: robot-motor-holder
License: All rights reserved
LicenseURL: https://en.wikipedia.org/wiki/All_rights_reserved
objects: Sketcher::SketchObject×7, PartDesign::Plane×6, PartDesign::Pad×4, App::Link×2, PartDesign::Pocket×2, PartDesign::AdditiveLoft×1, PartDesign::Mirrored×1, PartDesign::Body×1, App::LinkGroup×1
note: 29 computed .brp shape members not serialized (recipe doc carries the construction recipe); baked Part::Feature solids carry a one-line shape summary decoded from their .brp
EXTERNAL_REF file=Off-the-shelf/GW1812.FCStd obj=Body
EXTERNAL_REF file=robot-wheel.FCStd obj=Body

FEATURE [App::Link] Link  label="motor"
  LinkedObject = -> <external Off-the-shelf/GW1812.FCStd>#Body
FEATURE [PartDesign::Plane] DatumPlane
  AttachmentOffset = pos=(0,0,-4.1) rot=(0,0,1;0rad)
  Length = 60
  MapMode = 5
  Placement = pos=(-4.1,9e-16,-9e-16) rot=(0.57735,0.57735,0.57735;2.0944rad)
  ResizeMode = 0
  Support = -> [YZ_Plane]
  Width = 60
FEATURE [Sketcher::SketchObject] Sketch
  FullyConstrained = true
  MapMode = 5
  Placement = pos=(-4.1,9e-16,-9e-16) rot=(0.57735,0.57735,0.57735;2.0944rad)
  Support = -> [DatumPlane]
  sketch-geometry (14):
    g0: LineSegment StartX=-5.1 StartY=7 StartZ=0 EndX=5.1 EndY=7 EndZ=0
    g1: LineSegment StartX=5.1 StartY=7 StartZ=0 EndX=5.1 EndY=-7 EndZ=0
    g2: LineSegment StartX=5.1 StartY=-7 StartZ=0 EndX=-5.1 EndY=-7 EndZ=0
    g3: LineSegment StartX=-5.1 StartY=-7 StartZ=0 EndX=-5.1 EndY=7 EndZ=0
    g4: LineSegment StartX=-5.1 StartY=7 StartZ=0 EndX=-5.1 EndY=6.1 EndZ=0
    g5: LineSegment StartX=-5.1 StartY=6.1 StartZ=0 EndX=-3.9 EndY=6.1 EndZ=0
    g6: LineSegment StartX=-3.9 StartY=6.1 StartZ=0 EndX=-3.9 EndY=-6.1 EndZ=0
    g7: LineSegment StartX=-3.9 StartY=-6.1 StartZ=0 EndX=-5.1 EndY=-6.1 EndZ=0
    g8: LineSegment StartX=-5.1 StartY=-6.1 StartZ=0 EndX=-5.1 EndY=-7 EndZ=0
    g9: LineSegment StartX=5.1 StartY=7 StartZ=0 EndX=5.1 EndY=6.1 EndZ=0
    g10: LineSegment StartX=5.1 StartY=6.1 StartZ=0 EndX=3.9 EndY=6.1 EndZ=0
    g11: LineSegment StartX=3.9 StartY=6.1 StartZ=0 EndX=3.9 EndY=-6.1 EndZ=0
    g12: LineSegment StartX=3.9 StartY=-6.1 StartZ=0 EndX=5.1 EndY=-6.1 EndZ=0
    g13: LineSegment StartX=5.1 StartY=-6.1 StartZ=0 EndX=5.1 EndY=-7 EndZ=0
  constraints (39):
    c: Coincident(g0,g1)
    c: Coincident(g1,g2)
    c: Coincident(g2,g3)
    c: Coincident(g3,g0)
    c: Horizontal(g0)
    c: Horizontal(g2)
    c: Symmetric(g0,g1,g-1)
    c: DistanceX(g0,g0) = 10.2
    c: DistanceY(g2,g0) = 14
    c: Coincident(g0,g4)
    c: PointOnObject(g4,g3)
    c: Vertical(g4)
    c: Coincident(g4,g5)
    c: Horizontal(g5)
    c: Coincident(g5,g6)
    c: Vertical(g6)
    c: Coincident(g6,g7)
    c: PointOnObject(g7,g3)
    c: Horizontal(g7)
    c: Coincident(g7,g8)
    c: Coincident(g8,g2)
    c: DistanceY(g4,g4) = 0.9
    c: Coincident(g0,g9)
    c: PointOnObject(g9,g1)
    c: Vertical(g9)
    c: Coincident(g9,g10)
    c: Horizontal(g10)
    c: Coincident(g10,g11)
    c: Vertical(g11)
    c: Coincident(g11,g12)
    c: PointOnObject(g12,g1)
    c: Horizontal(g12)
    c: Coincident(g12,g13)
    c: Coincident(g13,g2)
    c: Equal(g9,g4)
    c: Equal(g4,g8)
    c: Equal(g8,g13)
    c: Equal(g7,g12)
    c: DistanceX(g5,g5) = 1.2
FEATURE [PartDesign::Pad] Pad
  Direction = (1,-1e-16,1e-16)
  Length = 18.4
  Length2 = 10
  Placement = pos=(-4.1,1e-15,-1e-15) rot=(0.57735,0.57735,0.57735;2.0944rad)
  Profile = -> Sketch
  ReferenceAxis = -> Sketch [N_Axis]
  Type = 0
FEATURE [PartDesign::Plane] DatumPlane001
  AttachmentOffset = pos=(0,0,0) rot=(0,0,1;1.5708rad)
  Length = 60
  MapMode = 5
  Placement = pos=(-4.1,-3.9,-2.3e-15) rot=(1,0,0;1.5708rad)
  ResizeMode = 0
  Support = -> [Pad]
  Width = 60
FEATURE [Sketcher::SketchObject] Sketch001
  FullyConstrained = false
  MapMode = 5
  Placement = pos=(-4.1,9e-16,-9e-16) rot=(0.57735,0.57735,0.57735;2.0944rad)
  Support = -> [DatumPlane]
  sketch-geometry (4):
    g0: LineSegment StartX=-5.1 StartY=7 StartZ=0 EndX=5.1 EndY=7 EndZ=0
    g1: LineSegment StartX=5.1 StartY=7 StartZ=0 EndX=5.1 EndY=-7 EndZ=0
    g2: LineSegment StartX=5.1 StartY=-7 StartZ=0 EndX=-5.1 EndY=-7 EndZ=0
    g3: LineSegment StartX=-5.1 StartY=-7 StartZ=0 EndX=-5.1 EndY=7 EndZ=0
  constraints (11):
    c: Coincident(g0,g1)
    c: Coincident(g1,g2)
    c: Coincident(g2,g3)
    c: Coincident(g3,g0)
    c: Horizontal(g0)
    c: Horizontal(g2)
    c: Vertical(g1)
    c: Vertical(g3)
    c: DistanceX(g0,g0) = 10.2
    c: DistanceY(g1,g1) = 14
    c: DistanceX(g0,g-1) = 5.1
FEATURE [PartDesign::Pad] Pad001
  BaseFeature = -> Pad
  Direction = (1,-1e-16,1e-16)
  Length = 2
  Length2 = 10
  Placement = pos=(-4.1,1e-15,-1e-15) rot=(0.57735,0.57735,0.57735;2.0944rad)
  Profile = -> Sketch001
  ReferenceAxis = -> Sketch001 [N_Axis]
  Reversed = true
  Type = 0
FEATURE [Sketcher::SketchObject] Sketch002
  FullyConstrained = true
  MapMode = 5
  Placement = pos=(-4.1,-3.9,-2.3e-15) rot=(1,0,0;1.5708rad)
  Support = -> [DatumPlane001]
  sketch-geometry (21):
    g0: Circle CenterX=1.5 CenterY=4.6 CenterZ=0 NormalX=0 NormalY=0 NormalZ=1 AngleXU=0 Radius=1
    g1: Circle CenterX=1.5 CenterY=-4.6 CenterZ=0 NormalX=0 NormalY=0 NormalZ=1 AngleXU=0 Radius=1
    g2: LineSegment StartX=1.5 StartY=4.6 StartZ=0 EndX=1.5 EndY=-4.6 EndZ=0
    g3: LineSegment StartX=0 StartY=5.01421 StartZ=0 EndX=0.5 EndY=5.01421 EndZ=0
    g4: LineSegment StartX=0.5 StartY=5.01421 StartZ=0 EndX=1.08579 EndY=5.6 EndZ=0
    g5: LineSegment StartX=1.08579 StartY=5.6 StartZ=0 EndX=1.91421 EndY=5.6 EndZ=0
    g6: LineSegment StartX=1.91421 StartY=5.6 StartZ=0 EndX=2.5 EndY=5.01421 EndZ=0
    g7: LineSegment StartX=2.5 StartY=5.01421 StartZ=0 EndX=20 EndY=5.01421 EndZ=0
    g8: LineSegment StartX=20 StartY=5.01421 StartZ=0 EndX=20 EndY=-6.1 EndZ=0
    g9: LineSegment StartX=20 StartY=-6.1 StartZ=0 EndX=6.58579 EndY=-6.1 EndZ=0
    g10: LineSegment StartX=6.58579 StartY=-6.1 StartZ=0 EndX=5.5 EndY=-5.01421 EndZ=0
    g11: LineSegment StartX=5.5 StartY=-5.01421 StartZ=0 EndX=2.5 EndY=-5.01421 EndZ=0
    g12: LineSegment StartX=2.5 StartY=-5.01421 StartZ=0 EndX=1.91421 EndY=-5.6 EndZ=0
    g13: LineSegment StartX=1.91421 StartY=-5.6 StartZ=0 EndX=1.08579 EndY=-5.6 EndZ=0
    g14: LineSegment StartX=1.08579 StartY=-5.6 StartZ=0 EndX=0.5 EndY=-5.01421 EndZ=0
    g15: LineSegment StartX=0.5 StartY=-5.01421 StartZ=0 EndX=0 EndY=-5.01421 EndZ=0
    g16: LineSegment StartX=0 StartY=-5.01421 StartZ=0 EndX=0 EndY=5.01421 EndZ=0
    g17: LineSegment StartX=2.5 StartY=5.01421 StartZ=0 EndX=15.8 EndY=5.01421 EndZ=0
    g18: LineSegment StartX=15.8 StartY=5.01421 StartZ=0 EndX=15.8 EndY=6.1 EndZ=0
    g19: LineSegment StartX=15.8 StartY=6.1 StartZ=0 EndX=20 EndY=6.1 EndZ=0
    g20: LineSegment StartX=20 StartY=6.1 StartZ=0 EndX=20 EndY=5.01421 EndZ=0
  constraints (58):
    c: Coincident(g2,g0)
    c: Coincident(g2,g1)
    c: Equal(g0,g1)
    c: Symmetric(g0,g1,g-1)
    c: Diameter(g0) = 2
    c: DistanceY(g1,g0) = 9.2
    c: DistanceX(g-1,g0) = 1.5
    c: PointOnObject(g3,g-2)
    c: Horizontal(g3)
    c: Coincident(g3,g4)
    c: Tangent(g4,g0)
    c: Coincident(g4,g5)
    c: Horizontal(g5)
    c: Coincident(g5,g6)
    c: Tangent(g6,g0)
    c: Coincident(g6,g7)
    c: Horizontal(g7)
    c: Coincident(g7,g8)
    c: Vertical(g8)
    c: Coincident(g8,g9)
    c: Horizontal(g9)
    c: Coincident(g9,g10)
    c: Coincident(g10,g11)
    c: Horizontal(g11)
    c: Coincident(g11,g12)
    c: Tangent(g12,g1)
    c: Coincident(g12,g13)
    c: Horizontal(g13)
    c: Coincident(g13,g14)
    c: Tangent(g14,g1)
    c: Coincident(g14,g15)
    c: Horizontal(g15)
    c: Coincident(g15,g16)
    c: Coincident(g16,g3)
    c: Symmetric(g3,g15,g-1)
    c: Angle(g4,g3) = 2.35619
    c: Equal(g4,g5)
    c: Equal(g5,g6)
    c: Tangent(g5,g0)
    c: PointOnObject(g3,g7)
    c: PointOnObject(g14,g11)
    c: Equal(g14,g13)
    c: Equal(g13,g12)
    c: Angle(g15,g14) = 2.35619
    c: DistanceX(g11,g11) = 3
    c: Angle(g9,g10) = 2.35619
    c: DistanceY(g9,g-1) = 6.1
    c: DistanceX(g-1,g7) = 20
    c: Coincident(g6,g17)
    c: PointOnObject(g17,g7)
    c: Coincident(g17,g18)
    c: Vertical(g18)
    c: Coincident(g18,g19)
    c: Horizontal(g19)
    c: Coincident(g19,g20)
    c: Coincident(g20,g8)
    c: Symmetric(g8,g19,g-1)
    c: DistanceX(g-1,g18) = 15.8
FEATURE [PartDesign::Pocket] Pocket
  BaseFeature = -> Pad001
  Direction = (2e-16,1,2e-16)
  Length = 5
  Length2 = 5
  Placement = pos=(-4.1,1e-15,-1e-15) rot=(0.57735,0.57735,0.57735;2.0944rad)
  Profile = -> Sketch002
  ReferenceAxis = -> Sketch002 [N_Axis]
  Type = 1
FEATURE [PartDesign::Plane] DatumPlane002
  Length = 60
  MapMode = 5
  Placement = pos=(14.3,1e-15,1.6e-15) rot=(0.57735,0.57735,0.57735;2.0944rad)
  ResizeMode = 0
  Support = -> [Pad]
  Width = 60
FEATURE [Sketcher::SketchObject] Sketch003
  FullyConstrained = true
  MapMode = 5
  Placement = pos=(14.3,1e-15,1.6e-15) rot=(0.57735,0.57735,0.57735;2.0944rad)
  Support = -> [DatumPlane002]
  sketch-geometry (8):
    g0: LineSegment StartX=-5.1 StartY=7 StartZ=0 EndX=5.1 EndY=7 EndZ=0
    g1: LineSegment StartX=5.1 StartY=7 StartZ=0 EndX=5.1 EndY=6.1 EndZ=0
    g2: LineSegment StartX=5.1 StartY=6.1 StartZ=0 EndX=-5.1 EndY=6.1 EndZ=0
    g3: LineSegment StartX=-5.1 StartY=6.1 StartZ=0 EndX=-5.1 EndY=7 EndZ=0
    g4: LineSegment StartX=-5.1 StartY=-6.1 StartZ=0 EndX=5.1 EndY=-6.1 EndZ=0
    g5: LineSegment StartX=5.1 StartY=-6.1 StartZ=0 EndX=5.1 EndY=-7 EndZ=0
    g6: LineSegment StartX=5.1 StartY=-7 StartZ=0 EndX=-5.1 EndY=-7 EndZ=0
    g7: LineSegment StartX=-5.1 StartY=-7 StartZ=0 EndX=-5.1 EndY=-6.1 EndZ=0
  constraints (22):
    c: Coincident(g0,g1)
    c: Coincident(g1,g2)
    c: Coincident(g2,g3)
    c: Coincident(g3,g0)
    c: Horizontal(g2)
    c: Vertical(g1)
    c: Vertical(g3)
    c: Coincident(g4,g5)
    c: Coincident(g5,g6)
    c: Coincident(g6,g7)
    c: Coincident(g7,g4)
    c: Horizontal(g4)
    c: Horizontal(g6)
    c: Vertical(g5)
    c: Vertical(g7)
    c: Equal(g3,g7)
    c: Equal(g4,g2)
    c: Symmetric(g0,g0,g-2)
    c: Symmetric(g0,g6,g-1)
    c: DistanceX(g0,g0) = 10.2
    c: DistanceY(g5,g0) = 14
    c: DistanceY(g1,g1) = 0.9
FEATURE [PartDesign::Plane] DatumPlane003
  AttachmentOffset = pos=(0,0,5) rot=(0,0,1;0rad)
  Length = 60
  MapMode = 5
  Placement = pos=(19.3,2.1e-15,2.7e-15) rot=(0.57735,0.57735,0.57735;2.0944rad)
  ResizeMode = 0
  Support = -> [DatumPlane002]
  Width = 60
FEATURE [Sketcher::SketchObject] Sketch004
  FullyConstrained = true
  MapMode = 5
  Placement = pos=(19.3,2.1e-15,2.7e-15) rot=(0.57735,0.57735,0.57735;2.0944rad)
  Support = -> [DatumPlane003]
  sketch-geometry (8):
    g0: ArcOfCircle CenterX=0 CenterY=0 CenterZ=0 NormalX=0 NormalY=0 NormalZ=1 AngleXU=0 Radius=6.1 StartAngle=0.580724 EndAngle=2.56087
    g1: ArcOfCircle CenterX=0 CenterY=0 CenterZ=0 NormalX=0 NormalY=0 NormalZ=1 AngleXU=0 Radius=6.1 StartAngle=3.72232 EndAngle=5.70246
    g2: LineSegment StartX=-5.1 StartY=3.34664 StartZ=0 EndX=-5.1 EndY=7 EndZ=0
    g3: LineSegment StartX=-5.1 StartY=7 StartZ=0 EndX=5.1 EndY=7 EndZ=0
    g4: LineSegment StartX=5.1 StartY=7 StartZ=0 EndX=5.1 EndY=3.34664 EndZ=0
    g5: LineSegment StartX=5.1 StartY=-3.34664 StartZ=0 EndX=5.1 EndY=-7 EndZ=0
    g6: LineSegment StartX=5.1 StartY=-7 StartZ=0 EndX=-5.1 EndY=-7 EndZ=0
    g7: LineSegment StartX=-5.1 StartY=-7 StartZ=0 EndX=-5.1 EndY=-3.34664 EndZ=0
  constraints (24):
    c: Coincident(g0,g-1)
    c: Coincident(g1,g0)
    c: Equal(g1,g0)
    c: Coincident(g0,g2)
    c: Coincident(g2,g3)
    c: Horizontal(g3)
    c: Coincident(g3,g4)
    c: Coincident(g4,g0)
    c: Coincident(g1,g5)
    c: Coincident(g5,g6)
    c: Coincident(g6,g7)
    c: Coincident(g7,g1)
    c: Vertical(g2)
    c: Vertical(g4)
    c: Vertical(g5)
    c: Vertical(g7)
    c: Horizontal(g6)
    c: Equal(g6,g3)
    c: Equal(g2,g4)
    c: Equal(g4,g7)
    c: Equal(g7,g5)
    c: DistanceX(g3,g3) = 10.2
    c: DistanceY(g5,g3) = 14
    c: Diameter(g0) = 12.2
FEATURE [PartDesign::AdditiveLoft] AdditiveLoft
  BaseFeature = -> Pocket
  Closed = false
  Placement = pos=(-4.1,1e-15,-1e-15) rot=(0.57735,0.57735,0.57735;2.0944rad)
  Profile = -> Sketch003
  Ruled = false
  Sections = -> [Sketch004]
FEATURE [PartDesign::Pad] Pad002
  BaseFeature = -> AdditiveLoft
  Direction = (1,0,-2e-16)
  Length = 8
  Length2 = 10
  Placement = pos=(-4.1,1e-15,-1e-15) rot=(0.57735,0.57735,0.57735;2.0944rad)
  Profile = -> Sketch004
  ReferenceAxis = -> Sketch004 [N_Axis]
  Type = 0
FEATURE [PartDesign::Mirrored] Mirrored
  BaseFeature = -> Pad002
  MirrorPlane = -> Sketch004 [H_Axis]
  Originals = -> [Pad002,AdditiveLoft]
  Placement = pos=(-4.1,1e-15,-1e-15) rot=(0.57735,0.57735,0.57735;2.0944rad)
FEATURE [PartDesign::Plane] DatumPlane004
  AttachmentOffset = pos=(0,0,0) rot=(0,0,1;1.5708rad)
  Length = 60
  MapMode = 5
  Placement = pos=(-4.1,2e-16,7) rot=(0,0,1;0rad)
  ResizeMode = 0
  Support = -> [Pad]
  Width = 60
FEATURE [App::Link] Link001  label="wheel"
  LinkPlacement = pos=(0,-19,0) rot=(0,0,1;0rad)
  LinkedObject = -> <external robot-wheel.FCStd>#Body
  Placement = pos=(0,-19,0) rot=(0,0,1;0rad)
FEATURE [PartDesign::Plane] DatumPlane005
  AttachmentOffset = pos=(0,0,0.5) rot=(0,0,1;0rad)
  Length = 60
  MapMode = 5
  Placement = pos=(0.5,-1e-16,1e-16) rot=(0.57735,0.57735,0.57735;2.0944rad)
  ResizeMode = 0
  Support = -> [YZ_Plane]
  Width = 60
FEATURE [Sketcher::SketchObject] Sketch005
  FullyConstrained = true
  MapMode = 5
  Placement = pos=(0.5,-1e-16,1e-16) rot=(0.57735,0.57735,0.57735;2.0944rad)
  Support = -> [DatumPlane005]
  sketch-geometry (8):
    g0: LineSegment StartX=0 StartY=8.73205 StartZ=0 EndX=-1 EndY=7 EndZ=0
    g1: LineSegment StartX=-1 StartY=7 StartZ=0 EndX=1 EndY=7 EndZ=0
    g2: LineSegment StartX=1 StartY=7 StartZ=0 EndX=0 EndY=8.73205 EndZ=0
    g3: Circle CenterX=0 CenterY=7.57735 CenterZ=0 NormalX=0 NormalY=0 NormalZ=1 AngleXU=0 Radius=1.1547
    g4: LineSegment StartX=0 StartY=-8.73205 StartZ=0 EndX=1 EndY=-7 EndZ=0
    g5: LineSegment StartX=1 StartY=-7 StartZ=0 EndX=-1 EndY=-7 EndZ=0
    g6: LineSegment StartX=-1 StartY=-7 StartZ=0 EndX=0 EndY=-8.73205 EndZ=0
    g7: Circle CenterX=0 CenterY=-7.57735 CenterZ=0 NormalX=0 NormalY=0 NormalZ=1 AngleXU=0 Radius=1.1547
  constraints (23):
    c: Coincident(g0,g1)
    c: Coincident(g1,g2)
    c: Coincident(g2,g0)
    c: Equal(g0,g1)
    c: Equal(g0,g2)
    c: PointOnObject(g0,g3)
    c: PointOnObject(g1,g3)
    c: PointOnObject(g2,g3)
    c: PointOnObject(g3,g-2)
    c: PointOnObject(g2,g-2)
    c: Coincident(g4,g5)
    c: Coincident(g5,g6)
    c: Coincident(g6,g4)
    c: Equal(g4,g5)
    c: Equal(g4,g6)
    c: PointOnObject(g4,g7)
    c: PointOnObject(g5,g7)
    c: PointOnObject(g6,g7)
    c: PointOnObject(g6,g-2)
    c: Equal(g7,g3)
    c: Symmetric(g7,g3,g-1)
    c: DistanceX(g1,g1) = 2
    c: DistanceY(g4,g1) = 14
FEATURE [PartDesign::Pad] Pad003
  BaseFeature = -> Mirrored
  Direction = (1,-1e-16,1e-16)
  Length = 21
  Length2 = 10
  Placement = pos=(-4.1,1e-15,-1e-15) rot=(0.57735,0.57735,0.57735;2.0944rad)
  Profile = -> Sketch005
  ReferenceAxis = -> Sketch005 [N_Axis]
  Type = 0
FEATURE [Sketcher::SketchObject] Sketch006
  FullyConstrained = true
  MapMode = 5
  Placement = pos=(-4.1,9e-16,-9e-16) rot=(0.57735,0.57735,0.57735;2.0944rad)
  Support = -> [DatumPlane]
  sketch-geometry (8):
    g0: LineSegment StartX=-5 StartY=6.1 StartZ=0 EndX=5 EndY=6.1 EndZ=0
    g1: LineSegment StartX=5 StartY=6.1 StartZ=0 EndX=5 EndY=6 EndZ=0
    g2: LineSegment StartX=5 StartY=6 StartZ=0 EndX=-5 EndY=6 EndZ=0
    g3: LineSegment StartX=-5 StartY=6 StartZ=0 EndX=-5 EndY=6.1 EndZ=0
    g4: LineSegment StartX=-5 StartY=-6 StartZ=0 EndX=5 EndY=-6 EndZ=0
    g5: LineSegment StartX=5 StartY=-6 StartZ=0 EndX=5 EndY=-6.1 EndZ=0
    g6: LineSegment StartX=5 StartY=-6.1 StartZ=0 EndX=-5 EndY=-6.1 EndZ=0
    g7: LineSegment StartX=-5 StartY=-6.1 StartZ=0 EndX=-5 EndY=-6 EndZ=0
  constraints (21):
    c: Coincident(g0,g1)
    c: Coincident(g1,g2)
    c: Coincident(g2,g3)
    c: Coincident(g3,g0)
    c: Horizontal(g2)
    c: Vertical(g1)
    c: Vertical(g3)
    c: Coincident(g4,g5)
    c: Coincident(g5,g6)
    c: Coincident(g6,g7)
    c: Coincident(g7,g4)
    c: Vertical(g5)
    c: Vertical(g7)
    c: Symmetric(g6,g5,g-2)
    c: Symmetric(g0,g0,g-2)
    c: DistanceX(g0,g0) = 10
    c: Equal(g3,g7)
    c: DistanceY(g7,g7) = 0.1
    c: Symmetric(g4,g2,g-1)
    c: DistanceY(g6,g0) = 12.2
    c: Horizontal(g4)
FEATURE [PartDesign::Pocket] Pocket001
  BaseFeature = -> Pad003
  Direction = (-1,1e-16,-1e-16)
  Length = 16
  Length2 = 5
  Placement = pos=(-4.1,1e-15,-1e-15) rot=(0.57735,0.57735,0.57735;2.0944rad)
  Profile = -> Sketch006
  ReferenceAxis = -> Sketch006 [N_Axis]
  Reversed = true
  Type = 0
FEATURE [PartDesign::Body] Body  label="motor-holder"
  Group = -> [DatumPlane,Sketch,Pad,DatumPlane001,Sketch001,Pad001,Sketch002,Pocket,DatumPlane002,Sketch003,DatumPlane003,Sketch004,AdditiveLoft,Pad002,Mirrored,DatumPlane004,DatumPlane005,Sketch005,Pad003,Sketch006,Pocket001]
  Origin = -> Origin
  Tip = -> Pocket001
FEATURE [App::LinkGroup] LinkGroup  label="traction-assy"
  ElementList = -> [Body,Link,Link001]
  LinkMode = 1
